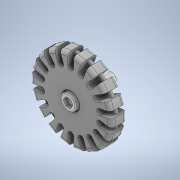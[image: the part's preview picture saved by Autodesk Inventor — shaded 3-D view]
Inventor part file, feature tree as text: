
AUTODESK INVENTOR PART (.ipt)
format: ipt  version: 2021 (Build 250183000, 183)  size: 569,344 bytes
history: native  units: mm
features: extrude x7, sketch x7, projected_geometry x2, pattern_circular x1, fillet x1
ambient origin geometry x8: Origin, YZ Plane, XZ Plane, XY Plane, X Axis, Y Axis, Z Axis, Center Point
bodies: Solid1 (feature_tree)
feature tree (18):
  extrude  "Extrusion1"  Depth=10.0mm
  extrude  "Extrusion2"  Depth=3.35mm
  extrude  "Extrusion3"  TaperAngle=0.0deg  [1 undecoded]
  pattern_circular  "Circular Pattern1"  Count=18 Angle=360.0deg
  extrude  "Extrusion4"  Depth=8.5mm
  extrude  "Extrusion5"  Depth=2.0mm
  extrude  "Extrusion6"  Depth=2.1mm
  extrude  "Extrusion7"  Depth=0.5mm TaperAngle=360.0deg
  fillet  "Fillet1"  Radius=8.5mm
  sketch  "Sketch1"  dims[d0=45.0mm d1=10.0mm]
  sketch  "Sketch2"  dims[d2=3.2mm d3=3.35mm]
  sketch  "Sketch3"  dims[d4=19.6mm d5=0.0mm d6=180.0mm d8=360.0deg]
  projected_geometry  "Projected Loop1"
  sketch  "Sketch4"  dims[d10=8.5mm d11=0.0mm d12=27.0mm]
  sketch  "Sketch5"  dims[d13=2.0mm d14=0.0mm d15=4.6mm]
  projected_geometry  "Projected Loop2"
  sketch  "Sketch6"  dims[d16=1.9mm d17=2.1mm]
  sketch  "Sketch7"  dims[d18=3.2mm d19=0.0mm d20=180.0mm d21=360.0deg d23=8.5mm d24=1.5mm d25=1.7mm d26=0.0mm d27=0.0mm d28=4.6mm d29=2.0mm d30=0.0mm d31=21.0mm d32=0.0mm d33=5.0mm d34=30.0mm d35=0.0mm d36=2.0mm d37=0.5mm]
note: 1 required parameter value undecoded (feature->parameter linkage not recoverable at this tier; creation-order binding heuristic only, values carry confidence <= 0.55)
